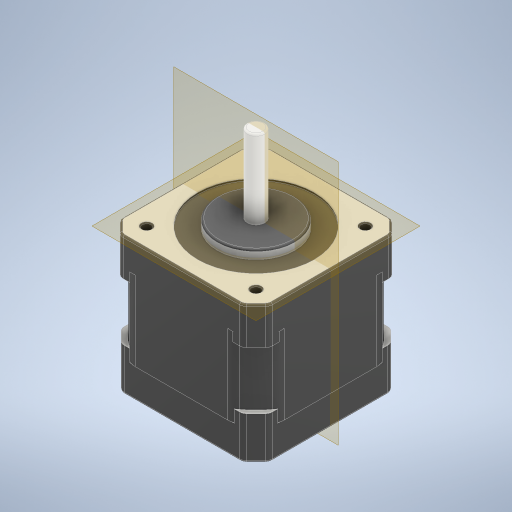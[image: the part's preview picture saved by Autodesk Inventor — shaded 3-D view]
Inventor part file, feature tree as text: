
AUTODESK INVENTOR PART (.ipt)
format: ipt  version: 2023 (Build 270158000, 158)  size: 746,496 bytes
history: native  units: in
note: dims shown in document units (in); Inventor stores cm internally (conversion verified against a paired STEP export)
features: direct_edit x3, move_body x3, other x1, sketch x1, revolve x1
ambient origin geometry x8: Origin, YZ Plane, XZ Plane, XY Plane, X Axis, Y Axis, Z Axis, Center Point
bodies: Solid1 (feature_tree)
feature tree (9):
  other  "NEMA_17_PHB42W40-401"
  direct_edit  "Direct Edit1"
  direct_edit  "Direct Edit2"
  direct_edit  "Direct Edit3"
  sketch  "Sketch1"  dims[d0=90.0deg d1=0.0in d2=0.0in d3=-0.8268in d4=0.0in d5=43.1791in d6=0.0in d7=0.0in d8=0.0in d9=-0.0295in]
  revolve  "Rotate1"  [1 undecoded]
  move_body  "Move1"
  move_body  "Move2"
  move_body  "Move3"
note: 1 required parameter value undecoded (feature->parameter linkage not recoverable at this tier; creation-order binding heuristic only, values carry confidence <= 0.55)
